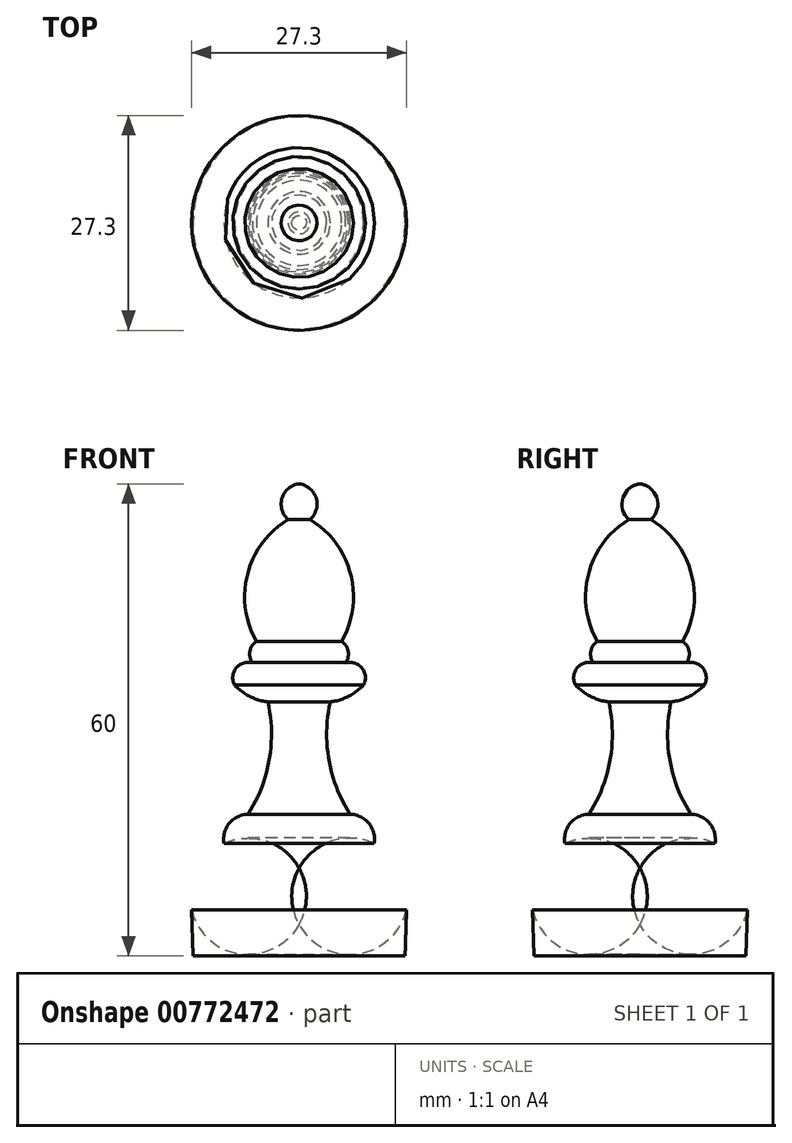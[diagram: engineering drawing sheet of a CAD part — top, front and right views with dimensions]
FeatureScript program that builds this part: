
annotation { "Feature Type Name" : "Feature", "Feature Type Description" : "" }
export const myFeature = defineFeature(function(context is Context, id is Id, definition is map)
    precondition{}
    {
        {
            var Q0;
            Q0=qCreatedBy(makeId("Front.planeOp"),FACE);
            var sketch = newSketch(context, id + "F0", { "sketchPlane" : qUnion([Q0])});
            skLineSegment(sketch, "E0", {"start": v(0, 0) * mm, "end": v(13.46, 0) * mm});
            skArc(sketch, "E1", {"start": v(13.65, 5.9) * mm, "mid": v(13.1, 10.84) * mm, "end": v(9.54, 14.31) * mm});
            skLineSegment(sketch, "E2", {"start": v(13.46, 0) * mm, "end": v(13.65, 5.9) * mm});
            skArc(sketch, "E3", {"start": v(9.54, 14.31) * mm, "mid": v(8.85, 16.86) * mm, "end": v(6.48, 18.02) * mm});
            skArc(sketch, "E4", {"start": v(3.97, 32.3) * mm, "mid": v(3.8, 24.9) * mm, "end": v(6.48, 18.02) * mm});
            skArc(sketch, "E5", {"start": v(3.97, 32.3) * mm, "mid": v(6.27, 32.99) * mm, "end": v(8.2, 34.43) * mm});
            skArc(sketch, "E6", {"start": v(8.2, 34.43) * mm, "mid": v(8, 36.59) * mm, "end": v(5.93, 37.24) * mm});
            skArc(sketch, "E7", {"start": v(5.93, 37.24) * mm, "mid": v(6.24, 38.72) * mm, "end": v(5.41, 40) * mm});
            skArc(sketch, "E8", {"start": v(5.41, 40) * mm, "mid": v(6.54, 48.55) * mm, "end": v(1.4, 55.46) * mm});
            skArc(sketch, "E9", {"start": v(1.4, 55.46) * mm, "mid": v(2.16, 58.18) * mm, "end": v(0, 60) * mm});
            skLineSegment(sketch, "E10", {"start": v(0, 60) * mm, "end": v(0, 0) * mm});
            skSolve(sketch);
        }
        {
            var Q0;
            Q0=makeQuery(id+"F0.imprint","IMPRINT",FACE,{"disambiguationData":[TD([[makeQuery(id+"F0.imprint","IMPRINT",EDGE,{"derivedFrom":sQuery(id+"F0.wireOp",EDGE,"E0")}),1.0]])]});
            var Q1;
            Q1=sQuery(id+"F0.wireOp",EDGE,"E10");
            revolve(context, id + "F1", {"surfaceOperationType" : NewSurfaceOperationType.NEW, "entities" : qUnion([Q0]), "axis" : qUnion([Q1]), "revolveType" : RevolveType.FULL});
        }
    });
